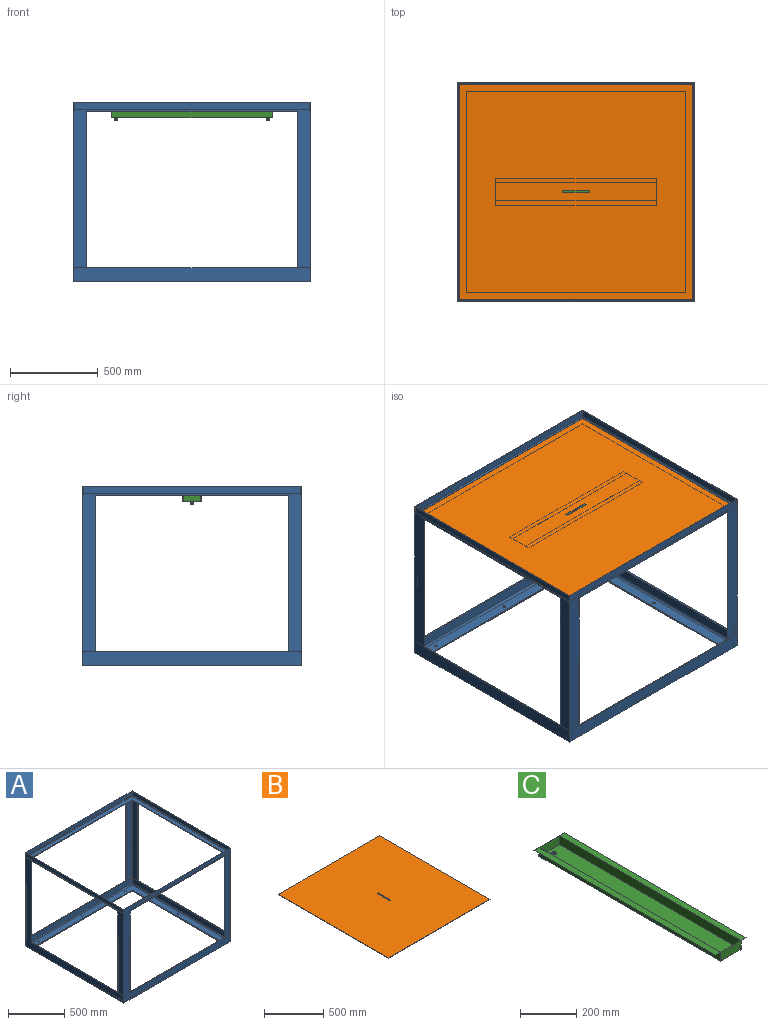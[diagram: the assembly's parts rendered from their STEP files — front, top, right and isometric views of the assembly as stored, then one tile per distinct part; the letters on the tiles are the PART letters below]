
ASSEMBLY  parts=3 mates=2
PART A: 93 faces, bbox 1346.2x1244.6x1016 mm
  f0: plane 1346.2x1244.6mm, normal (0,0,-1), area 249132.5mm2, adj f5,f6,f11,f12,f17,f18,f24,f25
  f1: cylinder r=1.6mm len=1241.43mm, axis (0,1,0), area 3082.7mm2, adj f2,f7,f19,f26
  f2: plane 1238.25x39.69mm, normal (1,0,0), area 49143mm2, adj f1,f3,f8,f20
  f3: cylinder r=6.35mm len=1238.25mm, axis (0,1,0), area 12305.1mm2, adj f2,f9,f21,f22
  f4: cylinder r=1.6mm len=1146.18mm, axis (0,1,0), area 2845.7mm2, adj f5,f10,f22,f23
  f5: plane 1143x1.59mm, normal (1,0,0), area 1814.5mm2, adj f0,f4,f11,f24
  f6: plane 1244.6x1016mm, normal (-1,0,0), area 293547.8mm2, adj f0,f12,f25,f26,f34,f37,f64,f83
  f7: cylinder r=1.6mm len=1343.03mm, axis (-1,0,0), area 3335.4mm2, adj f1,f8,f13,f26
  f8: plane 1339.85x39.69mm, normal (0,1,0), area 53175.3mm2, adj f2,f7,f9,f14
  f9: cylinder r=6.35mm len=1339.85mm, axis (-1,0,0), area 13318.5mm2, adj f3,f8,f15,f22
  f10: cylinder r=1.6mm len=1247.78mm, axis (-1,0,0), area 3098.4mm2, adj f4,f11,f16,f22
  f11: plane 1244.6x1.59mm, normal (0,1,0), area 1975.8mm2, adj f0,f5,f10,f17
  f12: plane 1346.2x1016mm, normal (0,-1,0), area 306451mm2, adj f0,f6,f18,f26,f28,f38,f45,f83
  f13: cylinder r=1.6mm len=1241.43mm, axis (0,-1,0), area 3082.7mm2, adj f7,f14,f19,f26
  f14: plane 1238.25x39.69mm, normal (-1,0,0), area 49143mm2, adj f8,f13,f15,f20
  f15: cylinder r=6.35mm len=1238.25mm, axis (0,-1,0), area 12305.1mm2, adj f9,f14,f21,f22
  f16: cylinder r=1.6mm len=1146.18mm, axis (0,-1,0), area 2845.7mm2, adj f10,f17,f22,f23
  f17: plane 1143x1.59mm, normal (-1,0,0), area 1814.5mm2, adj f0,f11,f16,f24
  f18: plane 1244.6x1016mm, normal (1,0,0), area 293547.8mm2, adj f0,f12,f25,f26,f46,f48,f56,f83
  f19: cylinder r=1.6mm len=1343.03mm, axis (1,0,0), area 3335.4mm2, adj f1,f13,f20,f26
  f20: plane 1339.85x39.69mm, normal (0,-1,0), area 53175.3mm2, adj f2,f14,f19,f21
  f21: cylinder r=6.35mm len=1339.85mm, axis (1,0,0), area 13318.5mm2, adj f3,f15,f20,f22
  f22: plane 1327.15x1225.55mm, normal (0,0,1), area 196320.2mm2, adj f3,f4,f9,f10,f15,f16,f21,f23
  f23: cylinder r=1.6mm len=1247.78mm, axis (1,0,0), area 3098.4mm2, adj f4,f16,f22,f24
  f24: plane 1244.6x1.59mm, normal (0,-1,0), area 1975.8mm2, adj f0,f5,f17,f23
  f25: plane 1346.2x1016mm, normal (0,1,0), area 306451mm2, adj f0,f6,f18,f26,f55,f58,f83,f84
  f26: plane 1346.2x1244.6mm, normal (0,0,1), area 8215.7mm2, adj f1,f6,f7,f12,f13,f18,f19,f25
  f27: plane 73.03x73.03mm, normal (0,0,-1), area 468.7mm2, adj f29,f30,f31,f32,f33,f35,f36
  f28: plane 889x3.18mm, normal (1,0,0), area 2822.6mm2, adj f0,f12,f29,f38
  f29: cylinder r=3.17mm len=889mm, axis (0,0,1), area 4433.7mm2, adj f0,f27,f28,f30,f35
  f30: plane 889x57.15mm, normal (0,1,0), area 50806.4mm2, adj f0,f27,f29,f31
  f31: cylinder r=9.52mm len=889mm, axis (0,0,1), area 13301.2mm2, adj f0,f27,f30,f32
  f32: plane 889x57.15mm, normal (1,0,0), area 50806.4mm2, adj f0,f27,f31,f33
  f33: cylinder r=3.17mm len=889mm, axis (0,0,1), area 4433.7mm2, adj f0,f27,f32,f34,f36
  f34: plane 889x3.18mm, normal (0,1,0), area 2822.6mm2, adj f0,f6,f33,f37
  f35: cylinder r=3.17mm len=1339.85mm, axis (-1,0,0), area 6662.1mm2, adj f27,f29,f36,f38,f39,f44,f47,f69
  f36: cylinder r=3.17mm len=1238.25mm, axis (0,1,0), area 6155.4mm2, adj f27,f33,f35,f37,f57,f63,f65,f77
  f37: plane 1092.2x3.18mm, normal (0,0,1), area 3467.7mm2, adj f6,f34,f36,f64
  f38: plane 1193.8x3.18mm, normal (0,0,1), area 3790.3mm2, adj f12,f28,f35,f45
  f39: plane 73.03x73.03mm, normal (0,0,-1), area 468.7mm2, adj f35,f40,f41,f42,f43,f44,f47
  f40: cylinder r=3.17mm len=889mm, axis (0,0,1), area 4433.7mm2, adj f0,f39,f41,f46,f47
  f41: plane 889x57.15mm, normal (-1,0,0), area 50806.4mm2, adj f0,f39,f40,f42
  f42: cylinder r=9.52mm len=889mm, axis (0,0,1), area 13301.2mm2, adj f0,f39,f41,f43
  f43: plane 889x57.15mm, normal (0,1,0), area 50806.3mm2, adj f0,f39,f42,f44
  f44: cylinder r=3.17mm len=889mm, axis (0,0,1), area 4433.7mm2, adj f0,f35,f39,f43,f45
  f45: plane 889x3.18mm, normal (-1,0,0), area 2822.6mm2, adj f0,f12,f38,f44
  f46: plane 889x3.18mm, normal (0,1,0), area 2822.6mm2, adj f0,f18,f40,f48
  f47: cylinder r=3.17mm len=1238.25mm, axis (0,-1,0), area 6155.4mm2, adj f35,f39,f40,f48,f49,f50,f73,f77
  f48: plane 1092.2x3.18mm, normal (0,0,1), area 3467.7mm2, adj f18,f46,f47,f56
  f49: plane 73.03x73.03mm, normal (0,0,-1), area 468.7mm2, adj f47,f50,f51,f52,f53,f54,f77
  f50: cylinder r=3.17mm len=889mm, axis (0,0,1), area 4433.7mm2, adj f0,f47,f49,f51,f56
  f51: plane 889x57.15mm, normal (-1,0,0), area 50806.3mm2, adj f0,f49,f50,f52
  f52: cylinder r=9.52mm len=889mm, axis (0,0,1), area 13301.2mm2, adj f0,f49,f51,f53
  f53: plane 889x57.15mm, normal (0,-1,0), area 50806.3mm2, adj f0,f49,f52,f54
  f54: cylinder r=3.17mm len=889mm, axis (0,0,1), area 4433.7mm2, adj f0,f49,f53,f55,f77
  f55: plane 889x3.18mm, normal (-1,0,0), area 2822.6mm2, adj f0,f25,f54,f84
  f56: plane 889x3.18mm, normal (0,-1,0), area 2822.6mm2, adj f0,f18,f48,f50
  f57: plane 73.03x73.03mm, normal (0,0,-1), area 468.7mm2, adj f36,f59,f60,f61,f62,f63,f77
  f58: plane 889x3.18mm, normal (1,0,0), area 2822.6mm2, adj f0,f25,f59,f84
  f59: cylinder r=3.17mm len=889mm, axis (0,0,1), area 4433.7mm2, adj f0,f57,f58,f60,f77
  f60: plane 889x57.15mm, normal (0,-1,0), area 50806.4mm2, adj f0,f57,f59,f61
  f61: cylinder r=9.52mm len=889mm, axis (0,0,1), area 13301.2mm2, adj f0,f57,f60,f62
  f62: plane 889x57.15mm, normal (1,0,0), area 50806.3mm2, adj f0,f57,f61,f63
  f63: cylinder r=3.17mm len=889mm, axis (0,0,1), area 4433.7mm2, adj f0,f36,f57,f62,f64
  f64: plane 889x3.18mm, normal (0,-1,0), area 2822.6mm2, adj f0,f6,f37,f63
  f65: plane 1231.9x57.15mm, normal (1,0,0), area 70403.1mm2, adj f36,f66,f69,f78
  f66: cylinder r=9.52mm len=1231.9mm, axis (0,1,0), area 18328.1mm2, adj f65,f70,f79,f80
  f67: cylinder r=3.17mm len=1098.55mm, axis (0,1,0), area 5458.7mm2, adj f68,f71,f80,f81
  f68: plane 1092.2x3.18mm, normal (1,0,0), area 3467.7mm2, adj f67,f72,f82,f83
  f69: plane 1333.5x57.15mm, normal (0,1,0), area 76209.5mm2, adj f35,f65,f70,f73
  f70: cylinder r=9.52mm len=1333.5mm, axis (-1,0,0), area 19848.3mm2, adj f66,f69,f74,f80
  f71: cylinder r=3.17mm len=1200.15mm, axis (-1,0,0), area 5965.4mm2, adj f67,f72,f75,f80
  f72: plane 1193.8x3.18mm, normal (0,1,0), area 3790.3mm2, adj f68,f71,f76,f83
  f73: plane 1231.9x57.15mm, normal (-1,0,0), area 70403.1mm2, adj f47,f69,f74,f78
  f74: cylinder r=9.52mm len=1231.9mm, axis (0,-1,0), area 18328.1mm2, adj f70,f73,f79,f80
  f75: cylinder r=3.17mm len=1098.55mm, axis (0,-1,0), area 5458.7mm2, adj f71,f76,f80,f81
  f76: plane 1092.2x3.18mm, normal (-1,0,0), area 3467.7mm2, adj f72,f75,f82,f83
  f77: cylinder r=3.17mm len=1339.85mm, axis (1,0,0), area 6662.1mm2, adj f36,f47,f49,f54,f57,f59,f78,f84
  f78: plane 1333.5x57.15mm, normal (0,-1,0), area 76209.5mm2, adj f65,f73,f77,f79
  f79: cylinder r=9.52mm len=1333.5mm, axis (1,0,0), area 19848.3mm2, adj f66,f74,f78,f80
  f80: plane 1314.45x1212.85mm, normal (0,0,1), area 274523.3mm2, adj f66,f67,f70,f71,f74,f75,f79,f81
  f81: cylinder r=3.17mm len=1200.15mm, axis (1,0,0), area 5965.4mm2, adj f67,f75,f80,f82
  f82: plane 1193.8x3.18mm, normal (0,-1,0), area 3790.3mm2, adj f68,f76,f81,f83
  f83: plane 1346.2x1244.6mm, normal (0,0,-1), area 370329.6mm2, adj f6,f12,f18,f25,f68,f72,f76,f82
  f84: plane 1193.8x3.18mm, normal (0,0,1), area 3790.3mm2, adj f25,f55,f58,f77
  f85: cylinder r=7.14mm len=14.29mm, axis (0,0,1), area 285mm2, adj f80,f83
  f86: cylinder r=7.14mm len=14.29mm, axis (0,0,1), area 285mm2, adj f80,f83
  f87: cylinder r=7.14mm len=14.29mm, axis (0,0,1), area 285mm2, adj f80,f83
  f88: cylinder r=7.14mm len=14.29mm, axis (0,0,1), area 285mm2, adj f80,f83
  f89: cylinder r=7.14mm len=14.29mm, axis (0,0,1), area 285mm2, adj f80,f83
  f90: cylinder r=7.14mm len=14.29mm, axis (0,0,1), area 285mm2, adj f80,f83
  f91: cylinder r=7.14mm len=14.29mm, axis (0,0,1), area 285mm2, adj f80,f83
  f92: cylinder r=7.14mm len=14.29mm, axis (0,0,1), area 285mm2, adj f80,f83
PART B: 10 faces, bbox 1219.2x1320.8x3.6 mm
  f0: plane 1320.8x1219.2mm, normal (0,0,1), area 1608383.9mm2, adj f2,f3,f4,f5,f6,f7,f8,f9
  f1: plane 1320.8x1219.2mm, normal (0,0,-1), area 1608383.9mm2, adj f2,f3,f4,f5,f6,f7,f8,f9
  f2: plane 1320.8x3.57mm, normal (-1,0,0), area 4717.7mm2, adj f0,f1,f3,f5
  f3: plane 1219.2x3.57mm, normal (0,-1,0), area 4354.8mm2, adj f0,f1,f2,f4
  f4: plane 1320.8x3.57mm, normal (1,0,0), area 4717.7mm2, adj f0,f1,f3,f5
  f5: plane 1219.2x3.57mm, normal (0,1,0), area 4354.8mm2, adj f0,f1,f2,f4
  f6: plane 152.4x3.57mm, normal (1,0,0), area 544.4mm2, adj f0,f1,f7,f9
  f7: plane 12.7x3.57mm, normal (0,-1,0), area 45.4mm2, adj f0,f1,f6,f8
  f8: plane 152.4x3.57mm, normal (-1,0,0), area 544.4mm2, adj f0,f1,f7,f9
  f9: plane 12.7x3.57mm, normal (0,1,0), area 45.4mm2, adj f0,f1,f6,f8
PART C: 39 faces, bbox 152.8x914.8x51.6 mm
  f0: plane 913.61x38.1mm, normal (1,0,0), area 34808.4mm2, adj f2,f10,f17,f18
  f1: plane 913.61x38.1mm, normal (-1,0,0), area 34808.4mm2, adj f2,f10,f17,f18
  f2: plane 913.61x101.6mm, normal (0,0,1), area 92487.3mm2, adj f0,f1,f17,f18,f20,f21
  f3: plane 914.4x0.4mm, normal (-1,0,0), area 362.9mm2, adj f4,f10,f11,f12
  f4: plane 914.4x25mm, normal (0,0,-1), area 22862.9mm2, adj f3,f5,f11,f12
  f5: plane 914.4x38.1mm, normal (-1,0,0), area 34838.6mm2, adj f4,f6,f11,f12
  f6: plane 914.4x102.39mm, normal (0,0,-1), area 93058.8mm2, adj f5,f7,f11,f12,f13,f15
  f7: plane 914.4x38.1mm, normal (1,0,0), area 34838.6mm2, adj f6,f8,f11,f12
  f8: plane 914.4x25mm, normal (0,0,-1), area 22862.9mm2, adj f7,f9,f11,f12
  f9: plane 914.4x0.4mm, normal (1,0,0), area 362.9mm2, adj f8,f10,f11,f12
  f10: plane 914.4x152.4mm, normal (0,0,1), area 46532.2mm2, adj f0,f1,f3,f9,f11,f12,f17,f18
  f11: plane 152.4x38.5mm, normal (0,1,0), area 3961.7mm2, adj f3,f4,f5,f6,f7,f8,f9,f10
  f12: plane 152.4x38.5mm, normal (0,-1,0), area 3961.7mm2, adj f3,f4,f5,f6,f7,f8,f9,f10
  f13: cylinder r=9.53mm len=19.05mm, axis (0,0,1), area 760.1mm2, adj f6,f14
  f14: plane 19.05x19.05mm, normal (0,0,-1), area 117.5mm2, adj f13,f19
  f15: cylinder r=9.53mm len=19.05mm, axis (0,0,1), area 760.1mm2, adj f6,f16
  f16: plane 19.05x19.05mm, normal (0,0,-1), area 117.5mm2, adj f15,f22
  f17: plane 101.6x38.1mm, normal (0,1,0), area 3871mm2, adj f0,f1,f2,f10
  f18: plane 101.6x38.1mm, normal (0,-1,0), area 3871mm2, adj f0,f1,f2,f10
  f19: cone r=4.76mm half-angle=45deg, axis (0,0,-1), area 136.2mm2, adj f14,f26,f28
  f20: cone r=4.76mm half-angle=45deg, axis (0,0,1), area 136.2mm2, adj f2,f27,f29
  f21: cone r=4.76mm half-angle=45deg, axis (0,0,1), area 136.2mm2, adj f2,f34,f36
  f22: cone r=4.76mm half-angle=45deg, axis (0,0,-1), area 136.2mm2, adj f16,f35,f37
  f23: bspline ~11.15x9.66mm, area 138.8mm2, adj f25,f26,f27,f28,f29,f30
  f24: bspline ~11.15x9.66mm, area 138.5mm2, adj f25,f26,f27,f28,f29,f30
  f25: bspline ~11.32x9.8mm, area 35.5mm2, adj f23,f24,f26,f27
  f26: plane 4.42x2.35mm, normal (0,0,1), area 0.4mm2, adj f19,f23,f24,f25
  f27: plane 3.59x3.53mm, normal (0,0,-1), area 0.4mm2, adj f20,f23,f24,f25
  f28: plane 9.92x9.91mm, normal (0,0,-1), area 11.9mm2, adj f19,f23,f24,f30
  f29: plane 9.91x9.91mm, normal (0,0,1), area 11.9mm2, adj f20,f23,f24,f30
  f30: cylinder r=3.97mm len=8.02mm, axis (0,0,-1), area 49.2mm2, adj f23,f24,f28,f29
  f31: bspline ~11.15x9.66mm, area 138.8mm2, adj f33,f34,f35,f36,f37,f38
  f32: bspline ~11.15x9.66mm, area 138.5mm2, adj f33,f34,f35,f36,f37,f38
  f33: bspline ~11.32x9.8mm, area 35.5mm2, adj f31,f32,f34,f35
  f34: plane 4.42x2.35mm, normal (0,0,-1), area 0.4mm2, adj f21,f31,f32,f33
  f35: plane 3.59x3.53mm, normal (0,0,1), area 0.4mm2, adj f22,f31,f32,f33
  f36: plane 9.92x9.91mm, normal (0,0,1), area 11.9mm2, adj f21,f31,f32,f38
  f37: plane 9.91x9.91mm, normal (0,0,-1), area 11.9mm2, adj f22,f31,f32,f38
  f38: cylinder r=3.97mm len=8.02mm, axis (0,0,1), area 49.2mm2, adj f31,f32,f36,f37
PLACE A t=(-91.32,-64.68,-161.1)mm fixed
PLACE B rot(axis=(0,0,1),90deg) t=(0.65,310.43,807.27)mm
PLACE C rot(axis=(0,0,-1),90deg) t=(-478.91,228.28,769.17)mm
MATE fastened B.f1 <-> C.f10  axis (0,0,-1) through (-21.71,218.73,807.27)mm
MATE fastened A.f22 <-> B.f1  axis (0,0,1) through (-21.71,218.73,807.27)mm
